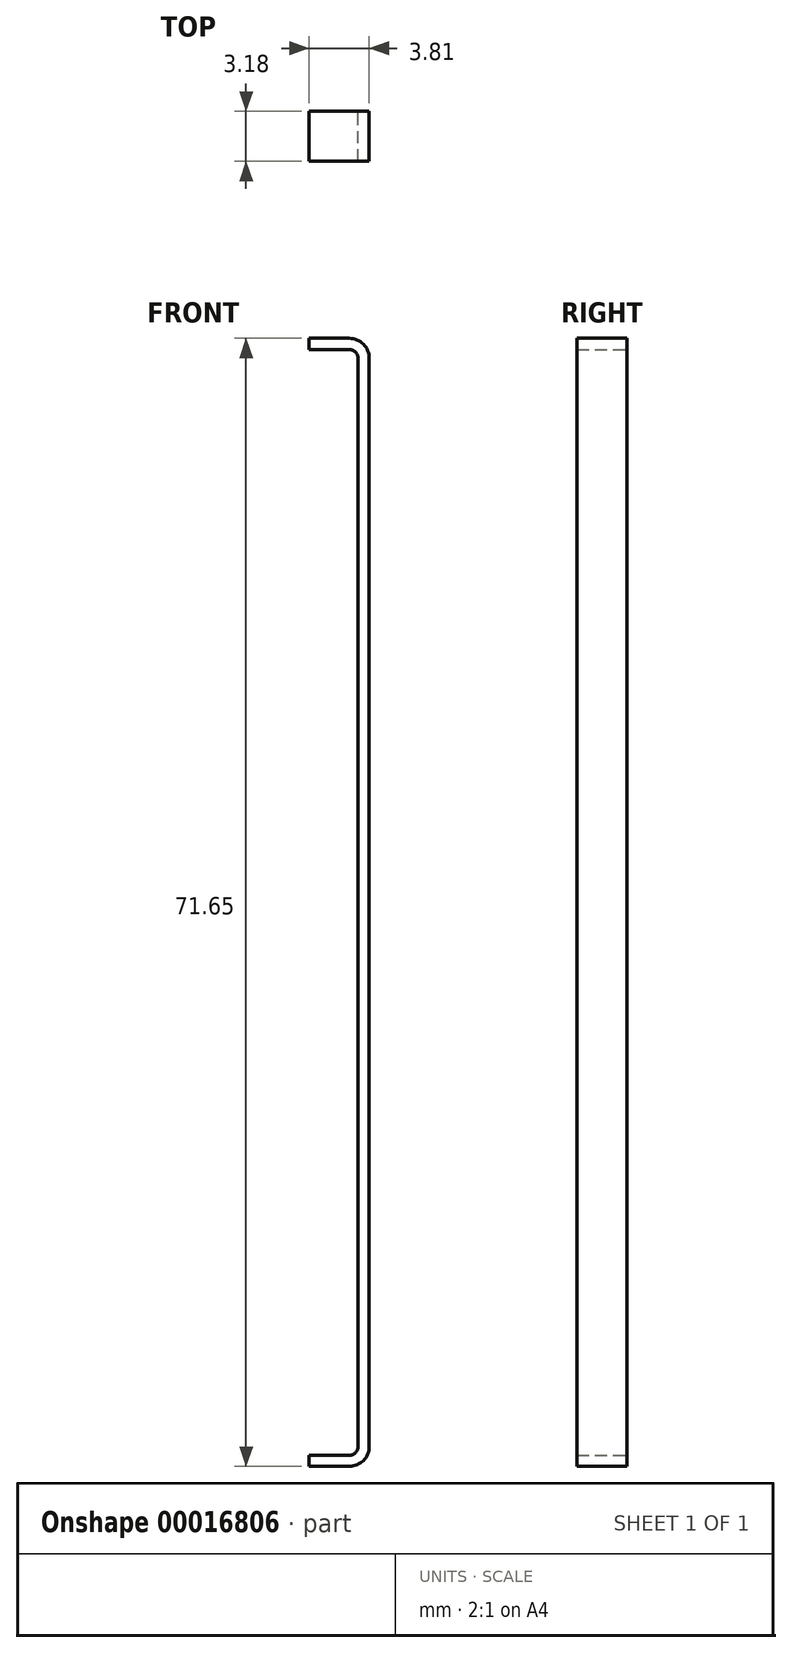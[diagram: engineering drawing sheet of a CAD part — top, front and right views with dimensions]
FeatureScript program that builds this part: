
annotation { "Feature Type Name" : "Feature", "Feature Type Description" : "" }
export const myFeature = defineFeature(function(context is Context, id is Id, definition is map)
    precondition{}
    {
        {
            var Q0;
            Q0=qCreatedBy(makeId("Front.planeOp"),FACE);
            var sketch = newSketch(context, id + "F0", { "sketchPlane" : qUnion([Q0])});
            skLineSegment(sketch, "E0", {"start": v(0, 0) * mm, "end": v(0, -71.65) * mm});
            skLineSegment(sketch, "E1", {"start": v(-0.71, -70.38) * mm, "end": v(-0.71, -1.27) * mm});
            skLineSegment(sketch, "E2", {"start": v(-3.8, -71.65) * mm, "end": v(-3.8, 0) * mm, "construction": true});
            skLineSegment(sketch, "E3.0", {"start": v(-0.71, 6.35) * mm, "end": v(-0.71, -63.5) * mm});
            skLineSegment(sketch, "E4", {"start": v(-3.8, -0.71) * mm, "end": v(-3.8, 0) * mm});
            skLineSegment(sketch, "E5", {"start": v(-1.27, -0.71) * mm, "end": v(-3.8, -0.71) * mm});
            skLineSegment(sketch, "E6", {"start": v(-3.81, 0) * mm, "end": v(0, 0) * mm});
            skLineSegment(sketch, "E7", {"start": v(0, -71.65) * mm, "end": v(-3.8, -71.65) * mm});
            skLineSegment(sketch, "E8", {"start": v(-3.8, -70.94) * mm, "end": v(-3.8, -71.65) * mm});
            skLineSegment(sketch, "E9", {"start": v(-1.27, -70.94) * mm, "end": v(-3.8, -70.94) * mm});
            skArc(sketch, "E10", {"start": v(-0.71, -1.27) * mm, "mid": v(-0.87, -0.87) * mm, "end": v(-1.27, -0.71) * mm});
            skLineSegment(sketch, "E11", {"start": v(-1.27, 0) * mm, "end": v(-1.27, -0.71) * mm, "construction": true});
            skLineSegment(sketch, "E12", {"start": v(0, -1.27) * mm, "end": v(-0.71, -1.27) * mm, "construction": true});
            skLineSegment(sketch, "E13", {"start": v(-1.27, -71.65) * mm, "end": v(-1.27, -70.94) * mm, "construction": true});
            skLineSegment(sketch, "E14", {"start": v(-0.71, -70.38) * mm, "end": v(0, -70.38) * mm, "construction": true});
            skArc(sketch, "E15", {"start": v(0, -1.27) * mm, "mid": v(-0.37, -0.37) * mm, "end": v(-1.27, 0) * mm});
            skArc(sketch, "E16", {"start": v(-1.27, -71.65) * mm, "mid": v(-0.37, -71.28) * mm, "end": v(0, -70.38) * mm});
            skArc(sketch, "E17.0", {"start": v(-1.27, -70.94) * mm, "mid": v(-0.87, -70.78) * mm, "end": v(-0.71, -70.38) * mm});
            skPoint(sketch, "E18", {"position": v(-0.71, 0) * mm});
            skLineSegment(sketch, "E19", {"start": v(-1.27, -0.71) * mm, "end": v(-0.71, -0.71) * mm, "construction": true});
            skSolve(sketch);
        }
        {
            var Q0;
            {var subQ6=sQuery(id+"F0.wireOp",EDGE,"E4");Q0=makeQuery(id+"F0.imprint","IMPRINT",FACE,{"disambiguationData":[TD([[makeQuery(id+"F0.imprint","IMPRINT",EDGE,{"derivedFrom":subQ6}),-1.0]])]});}
            var Q1;
            {var subQ9=sQuery(id+"F0.wireOp",EDGE,"E1");Q1=makeQuery(id+"F0.imprint","IMPRINT",FACE,{"disambiguationData":[TD([[makeQuery(id+"F0.imprint","IMPRINT",EDGE,{"derivedFrom":subQ9}),-1.0]])]});}
            extrude(context, id + "F1", {"entities" : qUnion([Q0, Q1]), "flatOperationType" : FlatOperationType.REMOVE, "offsetDistance" : 25.4 * mm, "depth" : 3.17 * mm, "domain" : OperationDomain.MODEL, "symmetric" : true});
        }
    });
